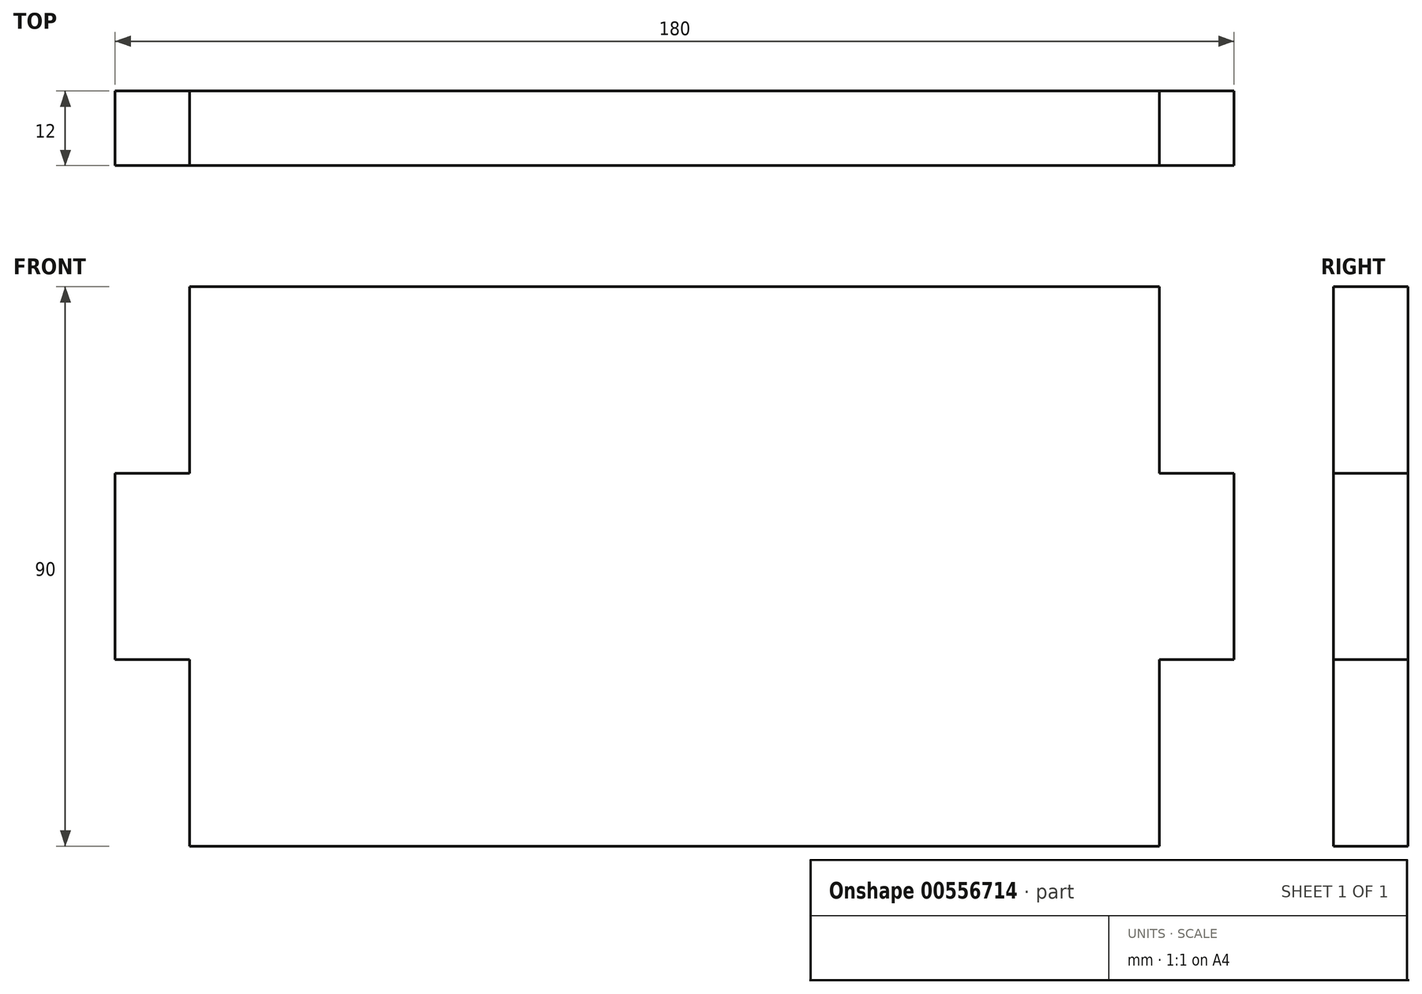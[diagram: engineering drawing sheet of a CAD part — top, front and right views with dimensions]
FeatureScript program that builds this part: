
annotation { "Feature Type Name" : "Feature", "Feature Type Description" : "" }
export const myFeature = defineFeature(function(context is Context, id is Id, definition is map)
    precondition{}
    {
        {
            var Q0;
            Q0=qCreatedBy(makeId("Front.planeOp"),FACE);
            var sketch = newSketch(context, id + "F0", { "sketchPlane" : qUnion([Q0])});
            skLineSegment(sketch, "E0", {"start": v(0, 0) * mm, "end": v(0, 30) * mm});
            skLineSegment(sketch, "E1", {"start": v(0, 30) * mm, "end": v(-12, 30) * mm});
            skLineSegment(sketch, "E2", {"start": v(-12, 30) * mm, "end": v(-12, 60) * mm});
            skLineSegment(sketch, "E3", {"start": v(-12, 60) * mm, "end": v(0, 60) * mm});
            skLineSegment(sketch, "E4", {"start": v(0, 60) * mm, "end": v(0, 90) * mm});
            skLineSegment(sketch, "E5", {"start": v(0, 90) * mm, "end": v(78, 90) * mm});
            skLineSegment(sketch, "E6", {"start": v(78, 90) * mm, "end": v(78, 0) * mm, "construction": true});
            skLineSegment(sketch, "E7", {"start": v(78, 0) * mm, "end": v(0, 0) * mm});
            skLineSegment(sketch, "E8.MirrorCS", {"start": v(156, 30) * mm, "end": v(168, 30) * mm});
            skLineSegment(sketch, "E9.MirrorCS", {"start": v(168, 30) * mm, "end": v(168, 60) * mm});
            skLineSegment(sketch, "E10.MirrorCS", {"start": v(156, 60) * mm, "end": v(156, 90) * mm});
            skLineSegment(sketch, "E11.MirrorCS", {"start": v(156, 0) * mm, "end": v(156, 30) * mm});
            skLineSegment(sketch, "E12.MirrorCS", {"start": v(156, 90) * mm, "end": v(78, 90) * mm});
            skLineSegment(sketch, "E13.MirrorCS", {"start": v(168, 60) * mm, "end": v(156, 60) * mm});
            skLineSegment(sketch, "E14.MirrorCS", {"start": v(78, 0) * mm, "end": v(156, 0) * mm});
            skSolve(sketch);
        }
        {
            var Q0;
            Q0=makeQuery(id+"F0.imprint","IMPRINT",FACE,{"disambiguationData":[TD([[makeQuery(id+"F0.imprint","IMPRINT",EDGE,{"derivedFrom":sQuery(id+"F0.wireOp",EDGE,"E0")}),-1.0]])]});
            extrude(context, id + "F1", {"entities" : qUnion([Q0]), "depth" : 12 * mm, "offsetDistance" : 25 * mm, "symmetric" : true});
        }
    });
